# Revit family: SDP-835 IP-видеокамера_RV17_LOD400 (08.12.23)
name_source: partatom
category: Устройства связи
revit_build: Autodesk Revit 2017 (Build: 20170118_1100(x64)
units: mm (PartAtom-declared; Revit-internal decimal feet)

## family parameters
Всегда вертикально = Нет
На основе рабочей плоскости = Да
Общий = Нет
При загрузке вырезать с полостями = Нет
Размер круглого соединителя = Использовать диаметр
Сохранять ориентацию аннотаций = Нет
Тип детали = Нормальный
Точка расчета площади = Нет

## types (1)
- SDP-835 IP-видеокамера
    ADSK_URL страницы изделия = https://stilsoft.ru
    ADSK_Единица измерения = шт.
    ADSK_Завод-изготовитель = ООО «Основа Безопасности»
    ADSK_Количество = 1
    ADSK_Марка = СТВФ.426459.173-02
    ADSK_Масса = 0.5
    ADSK_Наименование = IP-видеокамера SDP-835
    ADSK_Размер_Высота = 110 мм
    ADSK_Размер_ДиаметрИзделия = 140 мм
    d_короба = 20 мм
    Дальность ИК-подсветки, до, м = 30
    Диапазон рабочих температур, <unrecoverable-encoding: 5 bytes ef82b0d0a1> = от -40 до +50
    Матрица = 1/2,9" CMOS
    Мощность = 9
    Напряжение = 12
    Объектив, мм = 2.8 – 13,5
    Отметка по умолчанию = 1219 мм
    Поддерживаемые протоколы = TCP/IP, UDP, RTP, RTSP, RTCP, HTTP, DNS, DDNS, DHCP, FTP, NTP, PPPOE, SMTP, UPNP, ONVIF2.4.1
    Разрешение при частоте 25 кадр/сек, пикс. = 1920х1080
    Режим «День/ночь» = Механический ИК-фильтр с автопереключением
    Сетевой интерфейс = 1 RJ45 10М/100М Ethernet порт
    Скорость передачи = 32Кб/сек – 16МБ/сек
    Тип поддерживаемой карты памяти = SD-карта
    Угол обзора, ° = 20-86
    Управление = Веб-интерфейс, Stil-VL
    Формат сжатия = Н.264/MJPEG
    Чувствительность, Люкс = 0,001 / F1.2
    Электронный затвор, сек. = 1/5-1/50000
